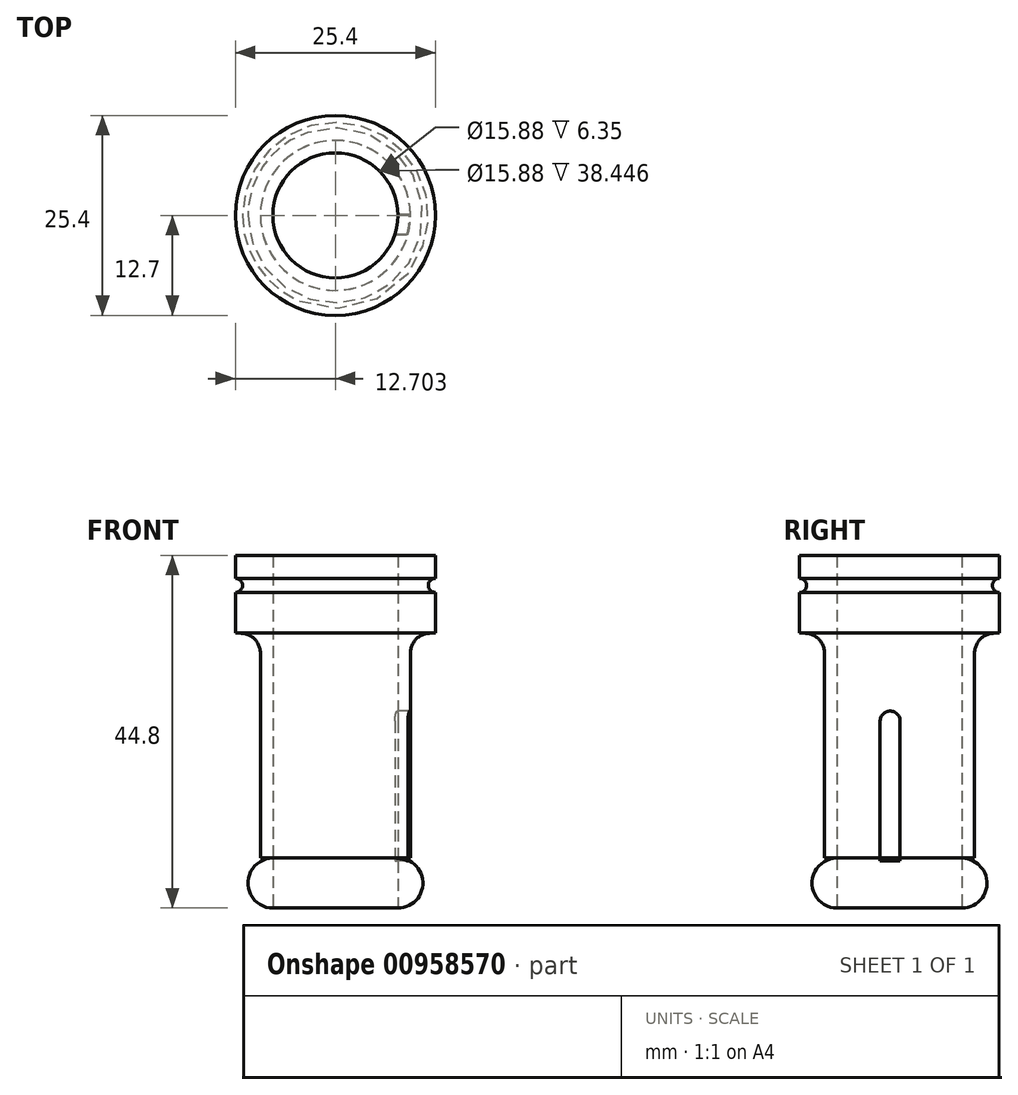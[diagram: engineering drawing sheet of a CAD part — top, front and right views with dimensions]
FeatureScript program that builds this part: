
annotation { "Feature Type Name" : "Feature", "Feature Type Description" : "" }
export const myFeature = defineFeature(function(context is Context, id is Id, definition is map)
    precondition{}
    {
        {
            var Q0;
            Q0=qCreatedBy(makeId("Front.planeOp"),FACE);
            var sketch = newSketch(context, id + "F0", { "sketchPlane" : qUnion([Q0])});
            skLineSegment(sketch, "E0", {"start": v(0, 0) * mm, "end": v(0, 6.35) * mm});
            skLineSegment(sketch, "E1", {"start": v(0, 6.35) * mm, "end": v(3.18, 6.35) * mm});
            skArc(sketch, "E2", {"start": v(0, 0) * mm, "mid": v(2.25, 0.93) * mm, "end": v(3.18, 3.18) * mm});
            skArc(sketch, "E3", {"start": v(3.18, 3.18) * mm, "mid": v(2.25, 5.42) * mm, "end": v(0, 6.35) * mm});
            skLineSegment(sketch, "E4", {"start": v(1.59, 6.35) * mm, "end": v(1.59, 34.93) * mm});
            skLineSegment(sketch, "E5", {"start": v(0, 6.35) * mm, "end": v(-15.88, 6.35) * mm});
            skLineSegment(sketch, "E6", {"start": v(-7.94, 6.35) * mm, "end": v(-7.94, 46.13) * mm});
            skLineSegment(sketch, "E7", {"start": v(0, 6.35) * mm, "end": v(0, 34.93) * mm});
            skLineSegment(sketch, "E8", {"start": v(0, 34.93) * mm, "end": v(1.59, 34.93) * mm});
            skLineSegment(sketch, "E9", {"start": v(1.59, 34.93) * mm, "end": v(4.76, 34.93) * mm});
            skLineSegment(sketch, "E10", {"start": v(4.76, 41) * mm, "end": v(4.76, 41) * mm});
            skArc(sketch, "E11", {"start": v(4.76, 41.9) * mm, "mid": v(3.86, 41) * mm, "end": v(4.76, 40.1) * mm});
            skLineSegment(sketch, "E12", {"start": v(4.76, 40.1) * mm, "end": v(4.76, 34.93) * mm});
            skLineSegment(sketch, "E13", {"start": v(4.76, 41.9) * mm, "end": v(4.76, 44.8) * mm});
            skLineSegment(sketch, "E14", {"start": v(4.76, 44.8) * mm, "end": v(0, 44.8) * mm});
            skLineSegment(sketch, "E15", {"start": v(0, 44.8) * mm, "end": v(0, 34.93) * mm});
            skSolve(sketch);
        }
        {
            var Q0;
            {var subQ2=sQuery(id+"F0.wireOp",EDGE,"E4");Q0=makeQuery(id+"F0.imprint","IMPRINT",FACE,{"disambiguationData":[TD([[makeQuery(id+"F0.imprint","IMPRINT",EDGE,{"derivedFrom":subQ2}),1.0]])]});}
            var Q1;
            Q1=makeQuery(id+"F0.imprint","IMPRINT",FACE,{"disambiguationData":[TD([[makeQuery(id+"F0.imprint","IMPRINT",EDGE,{"derivedFrom":sQuery(id+"F0.wireOp",EDGE,"E0")}),-1.0]])]});
            var Q2;
            Q2=makeQuery(id+"F0.imprint","IMPRINT",FACE,{"disambiguationData":[TD([[makeQuery(id+"F0.imprint","IMPRINT",EDGE,{"derivedFrom":sQuery(id+"F0.wireOp",EDGE,"E8")}),1.0]])]});
            var Q3;
            Q3=sQuery(id+"F0.wireOp",EDGE,"E6");
            revolve(context, id + "F1", {"surfaceOperationType" : NewSurfaceOperationType.NEW, "entities" : qUnion([Q0, Q1, Q2]), "axis" : qUnion([Q3]), "revolveType" : RevolveType.FULL});
        }
        {
            var Q0;
            Q0=makeQuery(id+"F1.opRevolve","SWEPT_EDGE",EDGE,{"disambiguationData":[OSD([sQuery(id+"F0.wireOp",EDGE,"E4"),sQuery(id+"F0.wireOp",EDGE,"E8"),sQuery(id+"F0.wireOp",EDGE,"E9")])]});
            fillet(context, id + "F2", {"entities" : qUnion([Q0]), "radius" : 2.54 * mm, "tangentPropagation" : true, "allowEdgeOverflow" : false});
        }
        {
            var Q0;
            Q0=qCreatedBy(makeId("Right.planeOp"),FACE);
            var sketch = newSketch(context, id + "F3", { "sketchPlane" : qUnion([Q0])});
            skLineSegment(sketch, "E16", {"start": v(-2.46, 5.98) * mm, "end": v(-2.46, 23.76) * mm});
            skLineSegment(sketch, "E17", {"start": v(-2.46, 5.98) * mm, "end": v(0.08, 5.98) * mm});
            skLineSegment(sketch, "E18", {"start": v(0.08, 5.98) * mm, "end": v(0.08, 23.76) * mm});
            skLineSegment(sketch, "E19", {"start": v(0.08, 23.76) * mm, "end": v(-2.46, 23.76) * mm});
            skArc(sketch, "E20", {"start": v(0.08, 23.76) * mm, "mid": v(-1.2, 25.03) * mm, "end": v(-2.46, 23.76) * mm});
            skSolve(sketch);
        }
        {
            var Q0;
            Q0=makeQuery(id+"F3.imprint","IMPRINT",FACE,{"disambiguationData":[TD([[makeQuery(id+"F3.imprint","IMPRINT",EDGE,{"derivedFrom":sQuery(id+"F3.wireOp",EDGE,"E16")}),-1.0]])]});
            var Q1;
            Q1=makeQuery(id+"F3.imprint","IMPRINT",FACE,{"disambiguationData":[TD([[makeQuery(id+"F3.imprint","IMPRINT",EDGE,{"derivedFrom":sQuery(id+"F3.wireOp",EDGE,"E19")}),-1.0]])]});
            extrude(context, id + "F4", {"entities" : qUnion([Q0, Q1]), "operationType" : NewBodyOperationType.REMOVE, "depth" : 25.4 * mm, "offsetDistance" : 25.4 * mm, "symmetric" : true});
        }
    });
